# Revit family: Electronics_Community-Subwoofers_Biamp_V2_212S
name_source: partatom
category: Communication Devices
units: mm (PartAtom-declared; Revit-internal decimal feet)

## family parameters
Cut with Voids When Loaded = No
Host = Face
Maintain Annotation Orientation = No
OmniClass Number = 23.85.10.11.14.14.14
Part Type = Normal
Room Calculation Point = No
Round Connector Dimension = Use Diameter
Shared = No

## types (2) — shared parameters
Connector Description = NL4, Terminal strip; 300W continuous, 750W program 34.6 volts RMS, 69.3 volts momentary peak
Default Elevation = 4' - 0"
Depth = 1' - 6"
Description = V2-212S Dual 12-Inch Subwoofer System
Driver Protection = DYNA-TECH protection circuitry
Drivers = LF 2 x 12-inch
Enclosure = 18mm, 11-ply cross-laminated birch
Frequency Response = 50 Hz to 125 Hz (-3 dB)
Height = 1' - 2"
Input Connection = NL4-compatible locking connector with terminal strip in parallel
Loudspeaker Type = Dual driver subwoofer, rectangular, vented bass
Manufacturer = Biamp
Maximum Output = 123 dB SPL / 129 dB SPL (peak)
Minimum Impedance = 4.2 ohms @ 110 Hz
Mounting/Rigging Provisions = 8 x M10 threaded rigging fittings
Nominal Impedance = 4 ohms
Nominal –6dB Beamwidth = 360° H x 180° V
Operating Range = 37 Hz to 500 Hz (-10 dB)
Optional Accessories = M10EYBLTKIT 10mm eyebolt kit; STKIT seat track kit
Product Documentation Link = https://downloads.biamp.com
Product Page URL = https://www.biamp.com
Product data url = https://www.bimobject.com
Recommended Signal Processing = 40 Hz, 24 dB/octave high pass filter
Sensitivity (1W/1m) = 98 dB  (50 Hz to  200 Hz) half space
URL = https://www.biamp.com
Weight = 70.00 lbf
Width = 3' - 0"

## per-type parameters (varying)
| type | Grill Material | Housing Material |
| V2-212S B | Biamp - Plastic - Black(Grid) | Biamp - Plastic - Black |
| V2-212S W | Biamp - Plastic - White(Grid) | Biamp - Plastic - White |

note: column(s) folded — value = type name in every type: Model

## geometry (parser evidence)
native form markers: Sweep x1
no freeform markers — native parametric forms only
